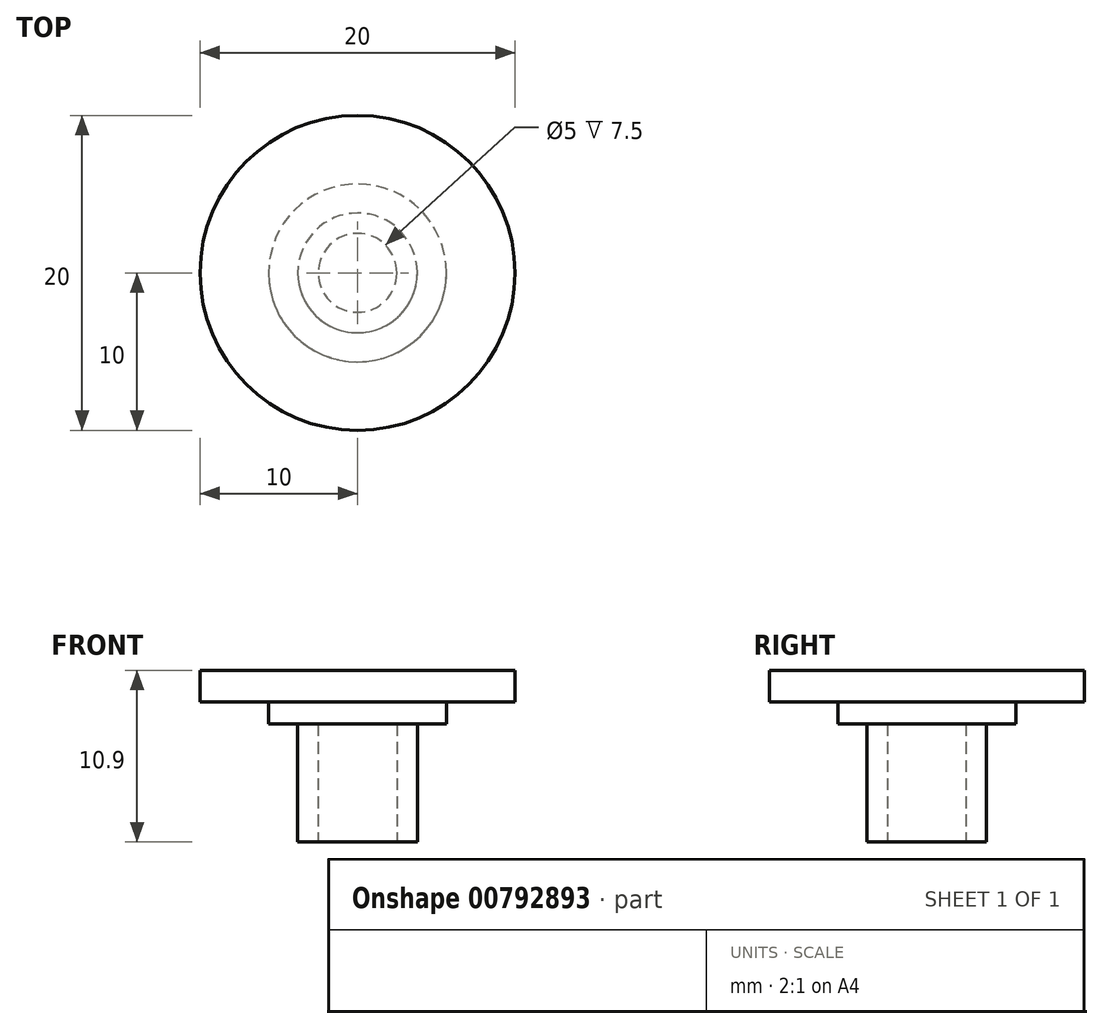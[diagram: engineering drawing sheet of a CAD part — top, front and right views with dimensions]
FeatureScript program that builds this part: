
annotation { "Feature Type Name" : "Feature", "Feature Type Description" : "" }
export const myFeature = defineFeature(function(context is Context, id is Id, definition is map)
    precondition{}
    {
        {
            var Q0;
            Q0=qCreatedBy(makeId("Top.planeOp"),FACE);
            var sketch = newSketch(context, id + "F0", { "sketchPlane" : qUnion([Q0])});
            skCircle(sketch, "E0", {"center": v(0, 0) * mm, "radius": 3.8 * mm});
            skSolve(sketch);
        }
        {
            var Q0;
            Q0 = qSketchRegion(id + "F0", true);
            extrude(context, id + "F1", {"entities" : qUnion([Q0]), "depth" : 8.9 * mm, "offsetDistance" : 25 * mm});
        }
        {
            var Q0;
            Q0=makeQuery(id+"F1.opExtrude","CAP_FACE",FACE,{"disambiguationData":[OSD([sQuery(id+"F0.wireOp",EDGE,"E0")])],"isStart":false});
            var sketch = newSketch(context, id + "F2", { "sketchPlane" : qUnion([Q0])});
            skCircle(sketch, "E1", {"center": v(0, 0) * mm, "radius": 10 * mm});
            skSolve(sketch);
        }
        {
            var Q0;
            Q0 = qSketchRegion(id + "F2", true);
            extrude(context, id + "F3", {"entities" : qUnion([Q0]), "operationType" : NewBodyOperationType.ADD, "depth" : 2 * mm, "offsetDistance" : 25 * mm});
        }
        {
            var Q0;
            Q0=makeQuery(id+"F1.opExtrude","CAP_FACE",FACE,{"disambiguationData":[OSD([sQuery(id+"F0.wireOp",EDGE,"E0")])],"isStart":true});
            var sketch = newSketch(context, id + "F4", { "sketchPlane" : qUnion([Q0])});
            skCircle(sketch, "E2", {"center": v(0, 0) * mm, "radius": 2.5 * mm});
            skSolve(sketch);
        }
        {
            var Q0;
            Q0 = qSketchRegion(id + "F4", true);
            extrude(context, id + "F5", {"entities" : qUnion([Q0]), "operationType" : NewBodyOperationType.REMOVE, "oppositeDirection" : true, "depth" : 8.3 * mm, "offsetDistance" : 25 * mm});
        }
        {
            var Q0;
            Q0=makeQuery(id+"F3.opExtrude","CAP_FACE",FACE,{"disambiguationData":[OSD([sQuery(id+"F2.wireOp",EDGE,"E1")])],"isStart":true});
            var sketch = newSketch(context, id + "F6", { "sketchPlane" : qUnion([Q0])});
            skCircle(sketch, "E3", {"center": v(0, 0) * mm, "radius": 5.65 * mm});
            skSolve(sketch);
        }
        {
            var Q0;
            Q0 = qSketchRegion(id + "F6", true);
            extrude(context, id + "F7", {"entities" : qUnion([Q0]), "operationType" : NewBodyOperationType.ADD, "depth" : 1.4 * mm, "offsetDistance" : 25 * mm});
        }
    });
